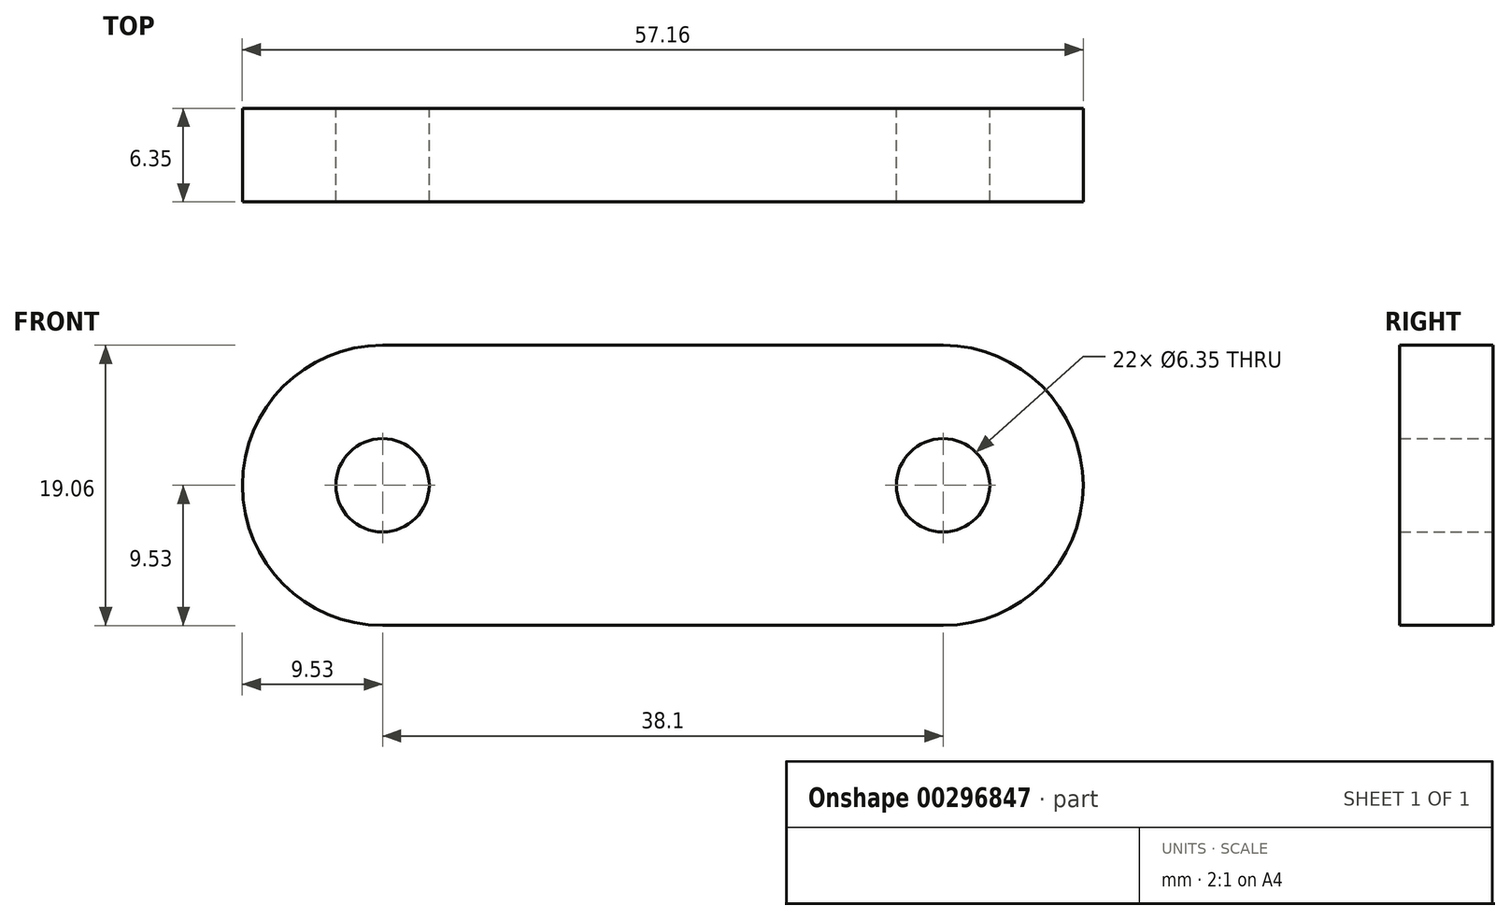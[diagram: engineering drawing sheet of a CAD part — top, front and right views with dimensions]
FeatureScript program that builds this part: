
annotation { "Feature Type Name" : "Feature", "Feature Type Description" : "" }
export const myFeature = defineFeature(function(context is Context, id is Id, definition is map)
    precondition{}
    {
        {
            var Q0;
            Q0=qCreatedBy(makeId("Front.planeOp"),FACE);
            var sketch = newSketch(context, id + "F0", { "sketchPlane" : qUnion([Q0])});
            skLineSegment(sketch, "E0.bottom", {"start": v(19.05, 9.53) * mm, "end": v(-19.05, 9.53) * mm});
            skLineSegment(sketch, "E0.top", {"start": v(19.05, -9.53) * mm, "end": v(-19.05, -9.53) * mm});
            skPoint(sketch, "E0.middle", {"position": v(0, 0) * mm});
            skArc(sketch, "E1", {"start": v(-19.05, 9.53) * mm, "mid": v(-28.58, 0) * mm, "end": v(-19.05, -9.53) * mm});
            skArc(sketch, "E2", {"start": v(19.05, -9.53) * mm, "mid": v(28.58, 0) * mm, "end": v(19.05, 9.53) * mm});
            skCircle(sketch, "E3", {"center": v(-19.05, 0) * mm, "radius": 3.18 * mm});
            skCircle(sketch, "E4", {"center": v(19.05, 0) * mm, "radius": 3.18 * mm});
            skSolve(sketch);
        }
        {
            var Q0;
            Q0 = qSketchRegion(id + "F0", true);
            extrude(context, id + "F1", {"entities" : qUnion([Q0]), "depth" : 6.35 * mm});
        }
    });
